# Revit family: record_DrDrver_DFA_Unhosted
name_source: partatom
category: Generic Models
revit_build: Autodesk Revit Architecture 2015 (Build: 20140606_1530(x64)
units: mm (PartAtom-declared; Revit-internal decimal feet)

## types (3) — shared parameters
AccessibilityPerformance = Pedestrian Access
AccessoryOptions = contact manufacturer
AcousticRating = none
ArmType = Standard arm(pushing only) or sliding arm (pulling/pushing)
Assembly Code = C1020410
AssetType = Fixed
Category = Pr_75_30_23_09: Automatic swing-door operators
Color = Stainless steel, aluminium, customer specific
Configuration = 1
Description = Automatic Swing Door Operator
DoorIncluded = 0
Double-LeafDoors = Yes
Double-LeafFireDoors = Yes
Double-LeafFireDoorsInformation = incl. mech. closing sequence control SFR 127, requires 108 mm height version
DriverHeight = 85 mm  [stored 0.278871 ft]
DriverLength = 600 mm
DriverMaterial = Aluminum
DriverWidth = 124 mm  [stored 0.406824 ft]
ElectronicLock = external
ExpectedLife = 10 years
HandicapAccessible = Yes
HasDrive = 1
HoldOpen = Yes
Infiltration = 0 CFM
IsExternal = No
IssueDate = (leave empty)
LintelDepth = If more than 330mm then max. 330mm and only standard arm - with 3 different sizes - can be used
Manufacturer = agtatec
ManufacturerURL = www.record.global
Material = Stainless steel (cover), aluminium (cover), plastics
ModelReference = Electro-mechanic door operator
NBSDescription = Door access controllers
Name = DFA 127
NominalHeight = 85 mm  [stored 0.278871 ft]
NominalLength = 600 mm
NominalWidth = 124 mm  [stored 0.406824 ft]
Operator = Wall installation or on door leaf
ReplacementCost = depends on the configuration and door type
SelfClosing = Yes
ServiceLifeDuration = 10-15 years
Shape = rectangular
SmokeStop = No
URL = www.record.global
Uniclass2 = PR_25_26_xx
Version = Version 1.0
WarrantyDescription = Depends on country
WarrantyDurationLabor = Depends on country
WarrantyDurationParts = Depends on country
WarrantyGuarantorLabor = Local door manufacturer
WarrantyGuarantorParts = Local door manufacturer
WarrantyStartDate = Depends on country
Weight = 0.00 kg
zero-valued in all types: GlazingAreaFraction, OperatorAndArmSystemHeightDifference, OperatorHeight, OperatorWidth

## per-type parameters (varying)
| type | A | B | C | FireExit | FireRating | Model | OpeningMechanism | ReferenceStandard |
| DFA 127 FP EU | 8 mm  [stored 0.0262467 ft] | 15 mm  [stored 0.0492126 ft] | 42.5 mm  [stored 0.139436 ft] | No |  | record DFA 127 IN automatic swing door operator | automatic | EN 16005, DIN 18650 |
| DFA 127 IN | 8 mm  [stored 0.0262467 ft] | 15 mm  [stored 0.0492126 ft] | 42.5 mm  [stored 0.139436 ft] | No |  | record DFA 127 IN automatic swing door operator | automatic | EN 16005, DIN 18650 |
| DFA 127 FP EU F (for fire doors) | 23 mm | 30 mm  [stored 0.0984252 ft] | 57.5 mm | Yes | n/a (depends on door leaf/frame only) | record DFA 127 automatic swing door operator for fire doors | automatic, manual | EN 16005, DIN 18650, EN 1154, EN 1155, EN 1158, DIN 18263-4 |

note: [stored X ft] marks values corroborated as IEEE doubles in the binary element streams (Revit-internal decimal feet)

## geometry (parser evidence)
native form markers: Sweep x3
no freeform markers — native parametric forms only
